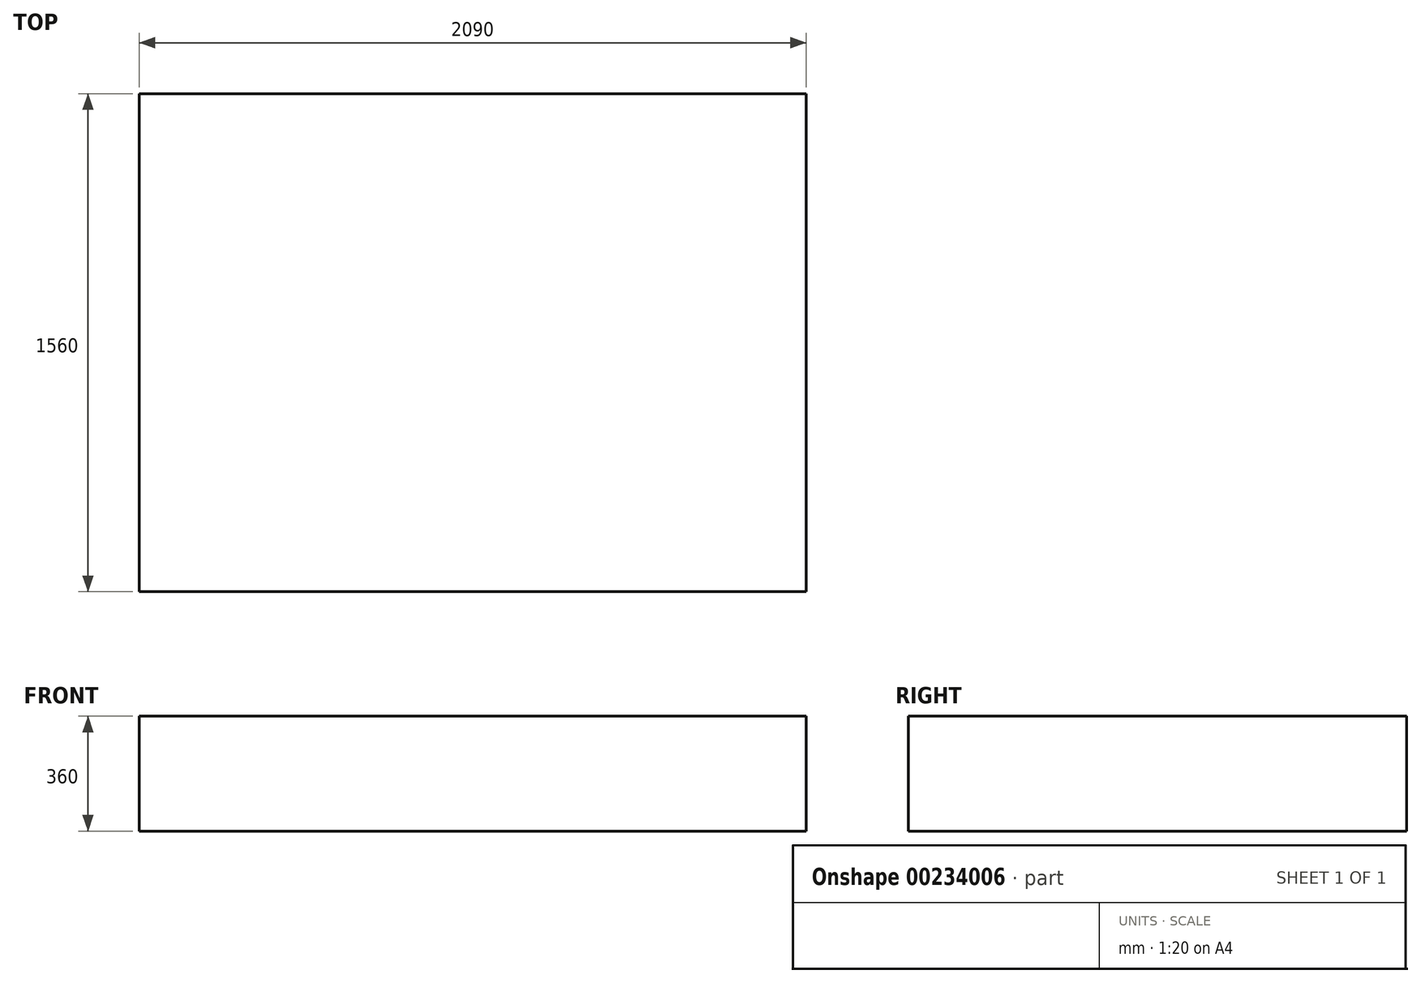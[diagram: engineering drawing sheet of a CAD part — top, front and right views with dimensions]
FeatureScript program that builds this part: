
annotation { "Feature Type Name" : "Feature", "Feature Type Description" : "" }
export const myFeature = defineFeature(function(context is Context, id is Id, definition is map)
    precondition{}
    {
        {
            var Q0;
            Q0=qCreatedBy(makeId("Top.planeOp"),FACE);
            var sketch = newSketch(context, id + "F0", { "sketchPlane" : qUnion([Q0])});
            skLineSegment(sketch, "E0.bottom", {"start": v(0, 0) * mm, "end": v(2090, 0) * mm});
            skLineSegment(sketch, "E0.top", {"start": v(0, -1560) * mm, "end": v(2090, -1560) * mm});
            skLineSegment(sketch, "E0.left", {"start": v(0, 0) * mm, "end": v(0, -1560) * mm});
            skLineSegment(sketch, "E0.right", {"start": v(2090, 0) * mm, "end": v(2090, -1560) * mm});
            skSolve(sketch);
        }
        {
            var Q0;
            Q0=makeQuery(id+"F0.imprint","IMPRINT",FACE,{"disambiguationData":[TD([[makeQuery(id+"F0.imprint","IMPRINT",EDGE,{"derivedFrom":sQuery(id+"F0.wireOp",EDGE,"E0.bottom")}),-1.0]])]});
            extrude(context, id + "F1", {"entities" : qUnion([Q0]), "depth" : 360 * mm, "offsetDistance" : 25 * mm});
        }
    });
